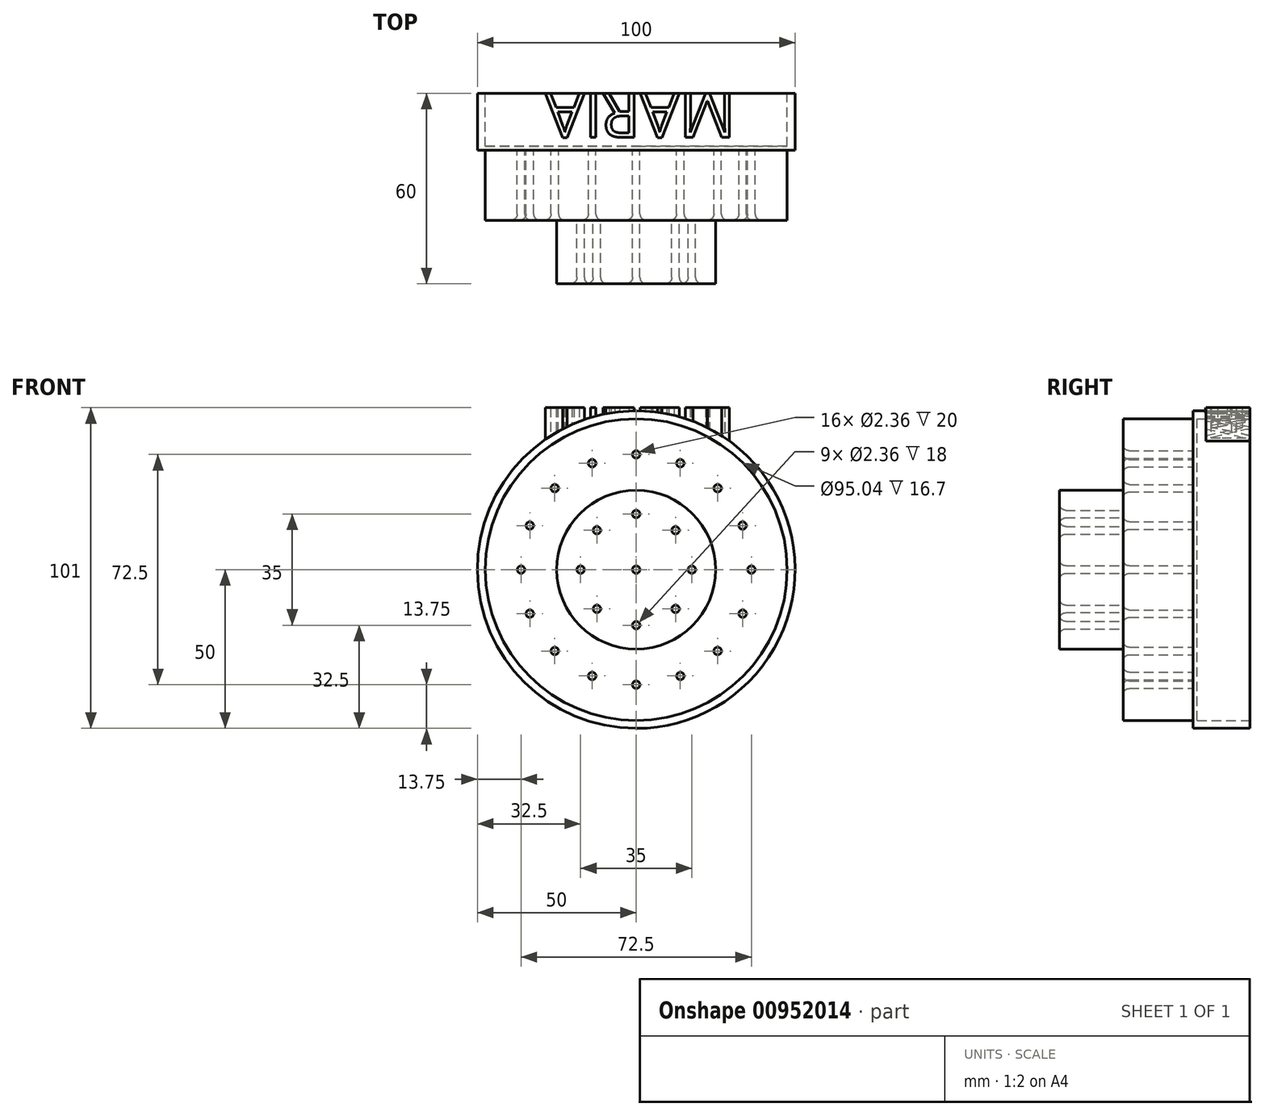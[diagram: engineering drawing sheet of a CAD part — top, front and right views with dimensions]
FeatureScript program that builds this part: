
annotation { "Feature Type Name" : "Feature", "Feature Type Description" : "" }
export const myFeature = defineFeature(function(context is Context, id is Id, definition is map)
    precondition{}
    {
        {
            var Q0;
            Q0=qCreatedBy(makeId("Front.planeOp"),FACE);
            var sketch = newSketch(context, id + "F0", { "sketchPlane" : qUnion([Q0])});
            skCircle(sketch, "E0", {"center": v(0, 0) * mm, "radius": 50 * mm});
            skSolve(sketch);
        }
        {
            var Q0;
            Q0=makeQuery(id+"F0.imprint","IMPRINT",FACE,{"disambiguationData":[TD([[makeQuery(id+"F0.imprint","IMPRINT",EDGE,{"derivedFrom":sQuery(id+"F0.wireOp",EDGE,"E0")}),1.0]])]});
            extrude(context, id + "F1", {"entities" : qUnion([Q0]), "depth" : 18 * mm, "offsetDistance" : 25 * mm});
        }
        {
            var Q0;
            Q0=makeQuery(id+"F1.opExtrude","CAP_FACE",FACE,{"disambiguationData":[OSD([sQuery(id+"F0.wireOp",EDGE,"E0")])],"isStart":false});
            var sketch = newSketch(context, id + "F2", { "sketchPlane" : qUnion([Q0])});
            skCircle(sketch, "E1", {"center": v(0, 0) * mm, "radius": 47.5 * mm});
            skCircle(sketch, "E2", {"center": v(0, 0) * mm, "radius": 36.25 * mm, "construction": true});
            skPoint(sketch, "E3", {"position": v(0, 36.25) * mm});
            skPoint(sketch, "E4", {"position": v(0, -36.25) * mm});
            skPoint(sketch, "E5", {"position": v(36.25, 0) * mm});
            skPoint(sketch, "E6", {"position": v(-36.25, 0) * mm});
            skLineSegment(sketch, "E7", {"start": v(0, 0) * mm, "end": v(-36.25, 0) * mm, "construction": true});
            skLineSegment(sketch, "E8", {"start": v(0, 0) * mm, "end": v(36.25, 0) * mm, "construction": true});
            skLineSegment(sketch, "E9", {"start": v(0, 0) * mm, "end": v(0, 36.25) * mm, "construction": true});
            skLineSegment(sketch, "E10", {"start": v(0, 0) * mm, "end": v(0, -36.25) * mm, "construction": true});
            skCircle(sketch, "E11", {"center": v(-36.25, 0) * mm, "radius": 1.18 * mm});
            skCircle(sketch, "E12", {"center": v(0, 36.25) * mm, "radius": 1.18 * mm});
            skCircle(sketch, "E13.MirrorC", {"center": v(36.25, 0) * mm, "radius": 1.18 * mm});
            skCircle(sketch, "E14.MirrorC", {"center": v(0, -36.25) * mm, "radius": 1.18 * mm});
            skLineSegment(sketch, "E15", {"start": v(0, 0) * mm, "end": v(25.63, 25.63) * mm, "construction": true});
            skLineSegment(sketch, "E16.MirrorCS", {"start": v(0, 0) * mm, "end": v(-25.63, 25.63) * mm, "construction": true});
            skLineSegment(sketch, "E17.MirrorCS", {"start": v(0, 0) * mm, "end": v(-25.63, -25.63) * mm, "construction": true});
            skLineSegment(sketch, "E18.MirrorCS", {"start": v(0, 0) * mm, "end": v(25.63, -25.63) * mm, "construction": true});
            skCircle(sketch, "E19", {"center": v(-25.63, 25.63) * mm, "radius": 1.18 * mm});
            skCircle(sketch, "E20", {"center": v(25.63, 25.63) * mm, "radius": 1.18 * mm});
            skCircle(sketch, "E21", {"center": v(25.63, -25.63) * mm, "radius": 1.18 * mm});
            skCircle(sketch, "E22", {"center": v(-25.63, -25.63) * mm, "radius": 1.18 * mm});
            skLineSegment(sketch, "E23", {"start": v(0, 0) * mm, "end": v(13.87, 33.5) * mm, "construction": true});
            skLineSegment(sketch, "E24.MirrorCS", {"start": v(0, 0) * mm, "end": v(-13.87, 33.5) * mm, "construction": true});
            skLineSegment(sketch, "E25.MirrorCS", {"start": v(0, 0) * mm, "end": v(-13.87, -33.5) * mm, "construction": true});
            skLineSegment(sketch, "E26.MirrorCS", {"start": v(0, 0) * mm, "end": v(13.87, -33.5) * mm, "construction": true});
            skLineSegment(sketch, "E27", {"start": v(0, 0) * mm, "end": v(33.5, 13.87) * mm, "construction": true});
            skLineSegment(sketch, "E28.MirrorCS", {"start": v(0, 0) * mm, "end": v(33.5, -13.87) * mm, "construction": true});
            skLineSegment(sketch, "E29.MirrorCS", {"start": v(0, 0) * mm, "end": v(-33.5, 13.87) * mm, "construction": true});
            skLineSegment(sketch, "E30.MirrorCS", {"start": v(0, 0) * mm, "end": v(-33.5, -13.87) * mm, "construction": true});
            skCircle(sketch, "E31", {"center": v(-33.5, 13.87) * mm, "radius": 1.18 * mm});
            skCircle(sketch, "E32", {"center": v(-13.87, 33.5) * mm, "radius": 1.18 * mm});
            skCircle(sketch, "E33.MirrorC", {"center": v(-13.87, -33.5) * mm, "radius": 1.18 * mm});
            skCircle(sketch, "E34.MirrorC", {"center": v(-33.5, -13.87) * mm, "radius": 1.18 * mm});
            skCircle(sketch, "E35.MirrorC", {"center": v(13.87, -33.5) * mm, "radius": 1.18 * mm});
            skCircle(sketch, "E36.MirrorC", {"center": v(33.5, -13.87) * mm, "radius": 1.18 * mm});
            skCircle(sketch, "E37.MirrorC", {"center": v(33.5, 13.87) * mm, "radius": 1.18 * mm});
            skCircle(sketch, "E38.MirrorC", {"center": v(13.87, 33.5) * mm, "radius": 1.18 * mm});
            skSolve(sketch);
        }
        {
            var Q0;
            Q0=makeQuery(id+"F2.imprint","IMPRINT",FACE,{"disambiguationData":[TD([[makeQuery(id+"F2.imprint","IMPRINT",EDGE,{"derivedFrom":sQuery(id+"F2.wireOp",EDGE,"E1")}),1.0]])]});
            extrude(context, id + "F3", {"entities" : qUnion([Q0]), "operationType" : NewBodyOperationType.ADD, "depth" : 22 * mm, "offsetDistance" : 25 * mm});
        }
        {
            var Q0;
            Q0=makeQuery(id+"F3.opExtrude","CAP_FACE",FACE,{"disambiguationData":[OSD([sQuery(id+"F2.wireOp",EDGE,"E1")])],"isStart":false});
            var sketch = newSketch(context, id + "F4", { "sketchPlane" : qUnion([Q0])});
            skCircle(sketch, "E39", {"center": v(0, 0) * mm, "radius": 25 * mm});
            skLineSegment(sketch, "E40", {"start": v(0, 0) * mm, "end": v(-25, 0) * mm, "construction": true});
            skLineSegment(sketch, "E41", {"start": v(0, 0) * mm, "end": v(25, 0) * mm, "construction": true});
            skLineSegment(sketch, "E42", {"start": v(0, 0) * mm, "end": v(0, 25) * mm, "construction": true});
            skLineSegment(sketch, "E43", {"start": v(0, 0) * mm, "end": v(0, -25) * mm, "construction": true});
            skLineSegment(sketch, "E44", {"start": v(0, 0) * mm, "end": v(17.68, 17.68) * mm, "construction": true});
            skLineSegment(sketch, "E45", {"start": v(0, 0) * mm, "end": v(23.1, 9.57) * mm, "construction": true});
            skLineSegment(sketch, "E46", {"start": v(0, 0) * mm, "end": v(9.57, 23.1) * mm, "construction": true});
            skLineSegment(sketch, "E47.MirrorCS", {"start": v(0, 0) * mm, "end": v(23.1, -9.57) * mm, "construction": true});
            skLineSegment(sketch, "E48.MirrorCS", {"start": v(0, 0) * mm, "end": v(17.68, -17.68) * mm, "construction": true});
            skLineSegment(sketch, "E49.MirrorCS", {"start": v(0, 0) * mm, "end": v(9.57, -23.1) * mm, "construction": true});
            skLineSegment(sketch, "E50.MirrorCS", {"start": v(0, 0) * mm, "end": v(-9.57, -23.1) * mm, "construction": true});
            skLineSegment(sketch, "E51.MirrorCS", {"start": v(0, 0) * mm, "end": v(-17.68, -17.68) * mm, "construction": true});
            skLineSegment(sketch, "E52.MirrorCS", {"start": v(0, 0) * mm, "end": v(-23.1, -9.57) * mm, "construction": true});
            skLineSegment(sketch, "E53.MirrorCS", {"start": v(0, 0) * mm, "end": v(-23.1, 9.57) * mm, "construction": true});
            skLineSegment(sketch, "E54.MirrorCS", {"start": v(0, 0) * mm, "end": v(-17.68, 17.68) * mm, "construction": true});
            skLineSegment(sketch, "E55.MirrorCS", {"start": v(0, 0) * mm, "end": v(-9.57, 23.1) * mm, "construction": true});
            skCircle(sketch, "E56", {"center": v(0, 0) * mm, "radius": 17.5 * mm, "construction": true});
            skPoint(sketch, "E57", {"position": v(0, 17.5) * mm});
            skPoint(sketch, "E58", {"position": v(6.7, 16.17) * mm});
            skPoint(sketch, "E59", {"position": v(12.37, 12.37) * mm});
            skPoint(sketch, "E60", {"position": v(16.17, 6.7) * mm});
            skPoint(sketch, "E61", {"position": v(17.5, 0) * mm});
            skPoint(sketch, "E62", {"position": v(16.17, -6.7) * mm});
            skPoint(sketch, "E63", {"position": v(12.37, -12.37) * mm});
            skPoint(sketch, "E64", {"position": v(6.7, -16.17) * mm});
            skPoint(sketch, "E65", {"position": v(0, -17.5) * mm});
            skPoint(sketch, "E66", {"position": v(-6.7, -16.17) * mm});
            skPoint(sketch, "E67", {"position": v(-12.37, -12.37) * mm});
            skPoint(sketch, "E68", {"position": v(-16.17, -6.7) * mm});
            skPoint(sketch, "E69", {"position": v(-17.5, 0) * mm});
            skPoint(sketch, "E70", {"position": v(-16.17, 6.7) * mm});
            skPoint(sketch, "E71", {"position": v(-12.37, 12.37) * mm});
            skPoint(sketch, "E72", {"position": v(-6.7, 16.17) * mm});
            skCircle(sketch, "E73", {"center": v(0, 17.5) * mm, "radius": 1.18 * mm});
            skCircle(sketch, "E74", {"center": v(-12.37, 12.37) * mm, "radius": 1.18 * mm});
            skCircle(sketch, "E75", {"center": v(-17.5, 0) * mm, "radius": 1.18 * mm});
            skCircle(sketch, "E76", {"center": v(-12.37, -12.37) * mm, "radius": 1.18 * mm});
            skCircle(sketch, "E77", {"center": v(0, -17.5) * mm, "radius": 1.18 * mm});
            skCircle(sketch, "E78", {"center": v(12.37, -12.37) * mm, "radius": 1.18 * mm});
            skCircle(sketch, "E79", {"center": v(17.5, 0) * mm, "radius": 1.18 * mm});
            skCircle(sketch, "E80", {"center": v(12.37, 12.37) * mm, "radius": 1.18 * mm});
            skCircle(sketch, "E81", {"center": v(0, 0) * mm, "radius": 1.18 * mm});
            skSolve(sketch);
        }
        {
            var Q0;
            Q0=makeQuery(id+"F4.imprint","IMPRINT",FACE,{"disambiguationData":[TD([[makeQuery(id+"F4.imprint","IMPRINT",EDGE,{"derivedFrom":sQuery(id+"F4.wireOp",EDGE,"E39")}),1.0]])]});
            extrude(context, id + "F5", {"entities" : qUnion([Q0]), "operationType" : NewBodyOperationType.ADD, "depth" : 20 * mm, "offsetDistance" : 25 * mm});
        }
        {
            var Q0;
            Q0=qCreatedBy(makeId("Top.planeOp"),FACE);
            var sketch = newSketch(context, id + "F6", { "sketchPlane" : qUnion([Q0])});
            skPoint(sketch, "E82", {"position": v(0, 0) * mm});
            skLineSegment(sketch, "E83", {"start": v(0, 0) * mm, "end": v(50, 0) * mm, "construction": true});
            skLineSegment(sketch, "E84", {"start": v(0, 0) * mm, "end": v(-50, 0) * mm, "construction": true});
            skText(sketch, "E85", { "text": "MARIA", "fontName": "OpenSans-Regular.ttf"});
            const initialGuessF6  = {"E85": [0.03122, 0, -1, 0, 0.01406]};
            skSetInitialGuess(sketch, initialGuessF6);
            skSolve(sketch);
        }
        {
            var Q0;
            Q0 = qSketchRegion(id + "F6", true);
            extrude(context, id + "F7", {"entities" : qUnion([Q0]), "operationType" : NewBodyOperationType.ADD, "depth" : 51 * mm, "offsetDistance" : 25 * mm});
        }
        {
            var Q0;
            Q0=makeQuery(id+"F3.opExtrude","CAP_EDGE",EDGE,{"disambiguationData":[OSD([sQuery(id+"F2.wireOp",EDGE,"E31")])],"isStart":false});
            var Q1;
            Q1=makeQuery(id+"F3.opExtrude","CAP_EDGE",EDGE,{"disambiguationData":[OSD([sQuery(id+"F2.wireOp",EDGE,"E11")])],"isStart":false});
            var Q2;
            Q2=makeQuery(id+"F3.opExtrude","CAP_EDGE",EDGE,{"disambiguationData":[OSD([sQuery(id+"F2.wireOp",EDGE,"E34.MirrorC")])],"isStart":false});
            var Q3;
            Q3=makeQuery(id+"F3.opExtrude","CAP_EDGE",EDGE,{"disambiguationData":[OSD([sQuery(id+"F2.wireOp",EDGE,"E22")])],"isStart":false});
            var Q4;
            Q4=makeQuery(id+"F3.opExtrude","CAP_EDGE",EDGE,{"disambiguationData":[OSD([sQuery(id+"F2.wireOp",EDGE,"E33.MirrorC")])],"isStart":false});
            var Q5;
            Q5=makeQuery(id+"F3.opExtrude","CAP_EDGE",EDGE,{"disambiguationData":[OSD([sQuery(id+"F2.wireOp",EDGE,"E14.MirrorC")])],"isStart":false});
            var Q6;
            Q6=makeQuery(id+"F3.opExtrude","CAP_EDGE",EDGE,{"disambiguationData":[OSD([sQuery(id+"F2.wireOp",EDGE,"E35.MirrorC")])],"isStart":false});
            var Q7;
            Q7=makeQuery(id+"F3.opExtrude","CAP_EDGE",EDGE,{"disambiguationData":[OSD([sQuery(id+"F2.wireOp",EDGE,"E21")])],"isStart":false});
            var Q8;
            Q8=makeQuery(id+"F3.opExtrude","CAP_EDGE",EDGE,{"disambiguationData":[OSD([sQuery(id+"F2.wireOp",EDGE,"E36.MirrorC")])],"isStart":false});
            var Q9;
            Q9=makeQuery(id+"F3.opExtrude","CAP_EDGE",EDGE,{"disambiguationData":[OSD([sQuery(id+"F2.wireOp",EDGE,"E13.MirrorC")])],"isStart":false});
            var Q10;
            Q10=makeQuery(id+"F3.opExtrude","CAP_EDGE",EDGE,{"disambiguationData":[OSD([sQuery(id+"F2.wireOp",EDGE,"E37.MirrorC")])],"isStart":false});
            var Q11;
            Q11=makeQuery(id+"F3.opExtrude","CAP_EDGE",EDGE,{"disambiguationData":[OSD([sQuery(id+"F2.wireOp",EDGE,"E20")])],"isStart":false});
            var Q12;
            Q12=makeQuery(id+"F3.opExtrude","CAP_EDGE",EDGE,{"disambiguationData":[OSD([sQuery(id+"F2.wireOp",EDGE,"E38.MirrorC")])],"isStart":false});
            var Q13;
            Q13=makeQuery(id+"F3.opExtrude","CAP_EDGE",EDGE,{"disambiguationData":[OSD([sQuery(id+"F2.wireOp",EDGE,"E12")])],"isStart":false});
            var Q14;
            Q14=makeQuery(id+"F3.opExtrude","CAP_EDGE",EDGE,{"disambiguationData":[OSD([sQuery(id+"F2.wireOp",EDGE,"E32")])],"isStart":false});
            var Q15;
            Q15=makeQuery(id+"F3.opExtrude","CAP_EDGE",EDGE,{"disambiguationData":[OSD([sQuery(id+"F2.wireOp",EDGE,"E19")])],"isStart":false});
            var Q16;
            Q16=makeQuery(id+"F5.opExtrude","CAP_EDGE",EDGE,{"disambiguationData":[OSD([sQuery(id+"F4.wireOp",EDGE,"E74")])],"isStart":false});
            var Q17;
            Q17=makeQuery(id+"F5.opExtrude","CAP_EDGE",EDGE,{"disambiguationData":[OSD([sQuery(id+"F4.wireOp",EDGE,"E75")])],"isStart":false});
            var Q18;
            Q18=makeQuery(id+"F5.opExtrude","CAP_EDGE",EDGE,{"disambiguationData":[OSD([sQuery(id+"F4.wireOp",EDGE,"E76")])],"isStart":false});
            var Q19;
            Q19=makeQuery(id+"F5.opExtrude","CAP_EDGE",EDGE,{"disambiguationData":[OSD([sQuery(id+"F4.wireOp",EDGE,"E77")])],"isStart":false});
            var Q20;
            Q20=makeQuery(id+"F5.opExtrude","CAP_EDGE",EDGE,{"disambiguationData":[OSD([sQuery(id+"F4.wireOp",EDGE,"E78")])],"isStart":false});
            var Q21;
            Q21=makeQuery(id+"F5.opExtrude","CAP_EDGE",EDGE,{"disambiguationData":[OSD([sQuery(id+"F4.wireOp",EDGE,"E79")])],"isStart":false});
            var Q22;
            Q22=makeQuery(id+"F5.opExtrude","CAP_EDGE",EDGE,{"disambiguationData":[OSD([sQuery(id+"F4.wireOp",EDGE,"E80")])],"isStart":false});
            var Q23;
            Q23=makeQuery(id+"F5.opExtrude","CAP_EDGE",EDGE,{"disambiguationData":[OSD([sQuery(id+"F4.wireOp",EDGE,"E73")])],"isStart":false});
            var Q24;
            Q24=makeQuery(id+"F5.opExtrude","CAP_EDGE",EDGE,{"disambiguationData":[OSD([sQuery(id+"F4.wireOp",EDGE,"E81")])],"isStart":false});
            fillet(context, id + "F8", {"entities" : qUnion([Q0, Q1, Q2, Q3, Q4, Q5, Q6, Q7, Q8, Q9, Q10, Q11, Q12, Q13, Q14, Q15, Q16, Q17, Q18, Q19, Q20, Q21, Q22, Q23, Q24]), "radius" : 2 * mm, "tangentPropagation" : true, "allowEdgeOverflow" : false});
        }
        {
            var Q0;
            Q0=qCreatedBy(makeId("Front.planeOp"),FACE);
            var sketch = newSketch(context, id + "F9", { "sketchPlane" : qUnion([Q0])});
            skCircle(sketch, "E86", {"center": v(0, 0) * mm, "radius": 47.52 * mm});
            skSolve(sketch);
        }
        {
            var Q0;
            Q0 = qSketchRegion(id + "F9", true);
            extrude(context, id + "F10", {"entities" : qUnion([Q0]), "operationType" : NewBodyOperationType.REMOVE, "depth" : 16.7 * mm, "offsetDistance" : 25 * mm});
        }
    });
